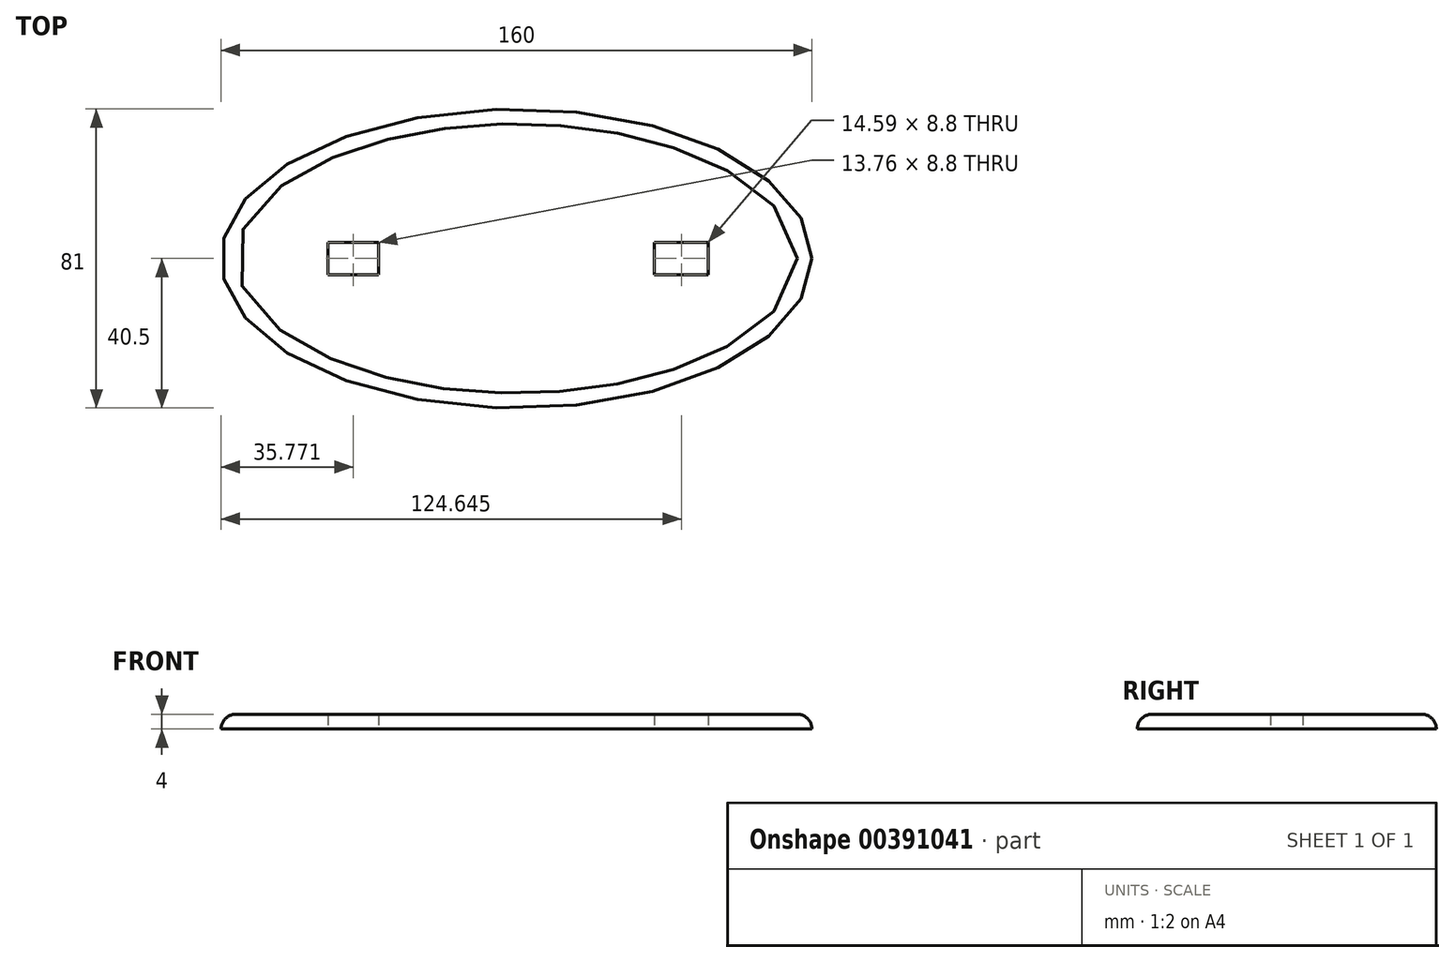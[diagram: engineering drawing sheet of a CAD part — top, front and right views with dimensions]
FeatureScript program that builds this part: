
annotation { "Feature Type Name" : "Feature", "Feature Type Description" : "" }
export const myFeature = defineFeature(function(context is Context, id is Id, definition is map)
    precondition{}
    {
        {
            var Q0;
            Q0=qCreatedBy(makeId("Top.planeOp"),FACE);
            var sketch = newSketch(context, id + "F0", { "sketchPlane" : qUnion([Q0])});
            skEllipse(sketch, "E0", {"center": v(0, 0) * mm, "majorRadius": 80 * mm, "minorRadius": 40.5 * mm, "majorAxis": v(1, 0)});
            skSolve(sketch);
        }
        {
            var Q0;
            Q0=makeQuery(id+"F0.imprint","IMPRINT",FACE,{"disambiguationData":[TD([[makeQuery(id+"F0.imprint","IMPRINT",EDGE,{"derivedFrom":sQuery(id+"F0.wireOp",EDGE,"E0")}),1.0]])]});
            extrude(context, id + "F1", {"entities" : qUnion([Q0]), "depth" : 4 * mm});
        }
        {
            var Q0;
            Q0=makeQuery(id+"F1.opExtrude","CAP_EDGE",EDGE,{"disambiguationData":[OSD([sQuery(id+"F0.wireOp",EDGE,"E0")])],"isStart":false});
            fillet(context, id + "F2", {"entities" : qUnion([Q0]), "radius" : 4 * mm, "tangentPropagation" : true, "allowEdgeOverflow" : false});
        }
        {
            var Q0;
            Q0=makeQuery(id+"F1.opExtrude","CAP_FACE",FACE,{"disambiguationData":[OSD([sQuery(id+"F0.wireOp",EDGE,"E0")])],"isStart":true});
            var sketch = newSketch(context, id + "F3", { "sketchPlane" : qUnion([Q0])});
            skLineSegment(sketch, "E1", {"start": v(37.35, 4.4) * mm, "end": v(37.35, -4.4) * mm});
            skLineSegment(sketch, "E2", {"start": v(37.35, -4.4) * mm, "end": v(51.94, -4.4) * mm});
            skLineSegment(sketch, "E3", {"start": v(51.94, -4.4) * mm, "end": v(51.94, 4.4) * mm});
            skLineSegment(sketch, "E4", {"start": v(51.94, 4.4) * mm, "end": v(37.35, 4.4) * mm});
            skLineSegment(sketch, "E5", {"start": v(-51.1, 4.4) * mm, "end": v(-51.1, -4.4) * mm});
            skLineSegment(sketch, "E6", {"start": v(-51.1, -4.4) * mm, "end": v(-37.35, -4.4) * mm});
            skLineSegment(sketch, "E7", {"start": v(-37.35, -4.4) * mm, "end": v(-37.35, 4.4) * mm});
            skLineSegment(sketch, "E8", {"start": v(-37.35, 4.4) * mm, "end": v(-51.1, 4.4) * mm});
            skPoint(sketch, "E9", {"position": v(0, 0) * mm});
            skSolve(sketch);
        }
        {
            var Q0;
            Q0 = qSketchRegion(id + "F3", true);
            var Q1;
            Q1=makeQuery(id+"F3.imprint","IMPRINT",FACE,{"disambiguationData":[TD([[makeQuery(id+"F3.imprint","IMPRINT",EDGE,{"derivedFrom":sQuery(id+"F3.wireOp",EDGE,"E5")}),1.0]])]});
            extrude(context, id + "F4", {"entities" : qUnion([Q0, Q1]), "operationType" : NewBodyOperationType.REMOVE, "oppositeDirection" : true, "depth" : 25 * mm});
        }
    });
